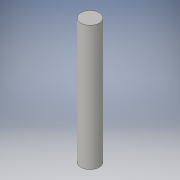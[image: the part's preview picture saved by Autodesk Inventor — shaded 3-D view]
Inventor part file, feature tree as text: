
AUTODESK INVENTOR PART (.ipt)
format: ipt  version: 2016 (Build 200138000, 138)  size: 84,992 bytes
history: native  units: in
note: dims shown in document units (in); Inventor stores cm internally (conversion verified against a paired STEP export)
features: extrude x1, sketch x1
ambient origin geometry x8: Origin, YZ Plane, XZ Plane, XY Plane, X Axis, Y Axis, Z Axis, Center Point
bodies: Solid1 (feature_tree)
feature tree (2):
  extrude  "Extrusion1"  Depth=1.0in TaperAngle=0.0deg
  sketch  "Sketch1"  dims[d0=0.146in d1=1.0in d2=0.0in]
